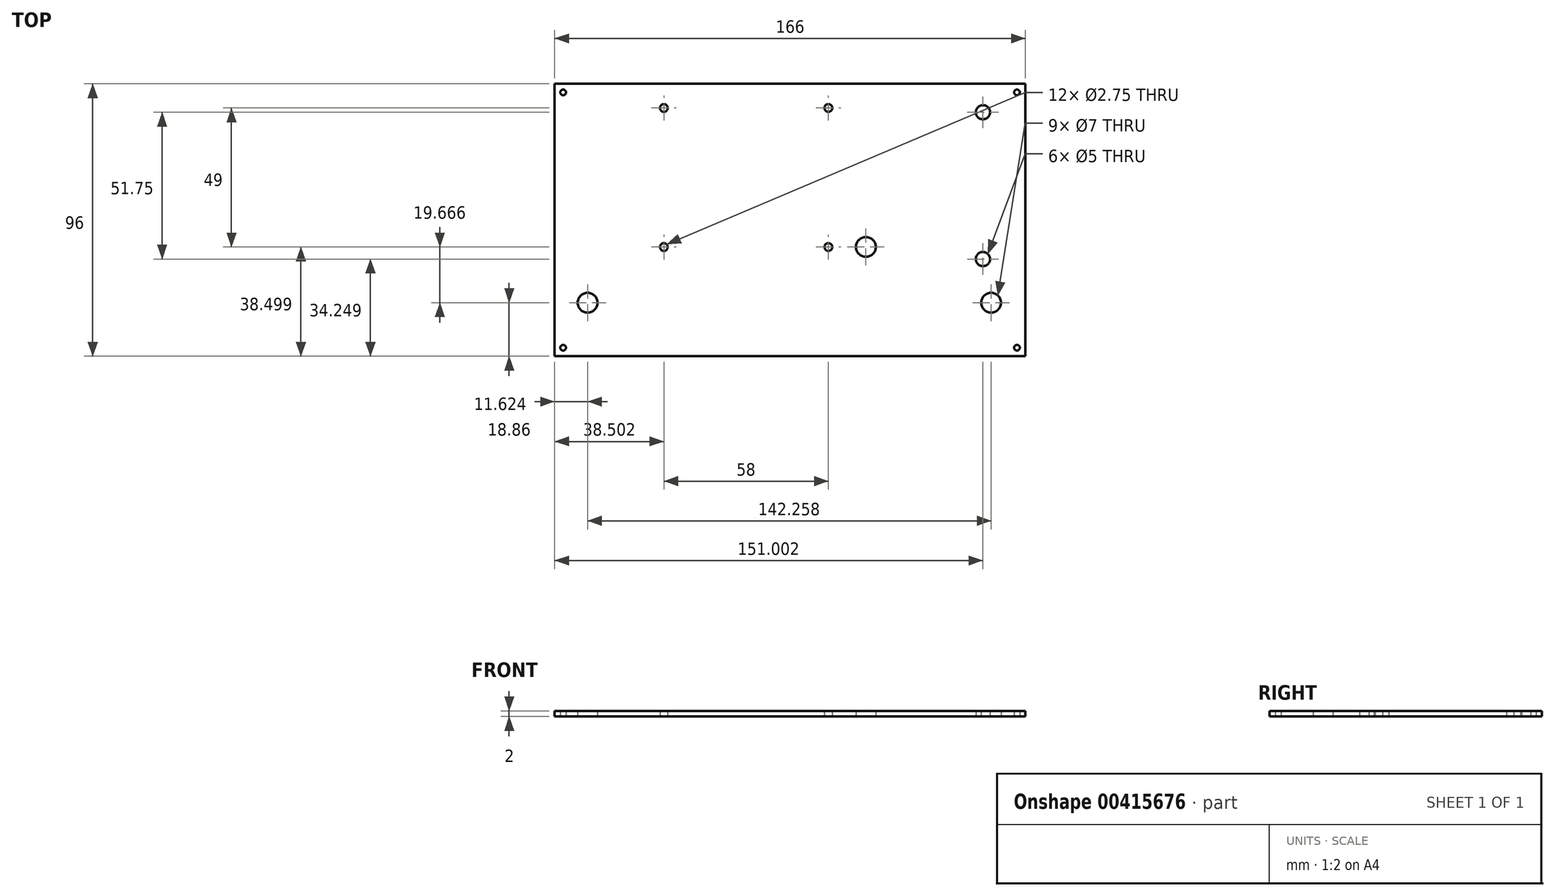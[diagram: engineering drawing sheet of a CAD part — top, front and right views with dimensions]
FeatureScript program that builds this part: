
annotation { "Feature Type Name" : "Feature", "Feature Type Description" : "" }
export const myFeature = defineFeature(function(context is Context, id is Id, definition is map)
    precondition{}
    {
        {
            var Q0;
            Q0=qCreatedBy(makeId("Top.planeOp"),FACE);
            var sketch = newSketch(context, id + "F0", { "sketchPlane" : qUnion([Q0])});
            skCircle(sketch, "E0", {"center": v(-64.72, 66.66) * mm, "radius": 1 * mm});
            skCircle(sketch, "E1", {"center": v(-64.72, -23.34) * mm, "radius": 1 * mm});
            skCircle(sketch, "E2", {"center": v(95.28, 66.66) * mm, "radius": 1 * mm});
            skCircle(sketch, "E3", {"center": v(95.28, -23.34) * mm, "radius": 1 * mm});
            skLineSegment(sketch, "E4.bottom", {"start": v(-67.72, 69.66) * mm, "end": v(98.28, 69.66) * mm});
            skLineSegment(sketch, "E4.top", {"start": v(-67.72, -26.34) * mm, "end": v(98.28, -26.34) * mm});
            skLineSegment(sketch, "E4.left", {"start": v(-67.72, 69.66) * mm, "end": v(-67.72, -26.34) * mm});
            skLineSegment(sketch, "E4.right", {"start": v(98.28, 69.66) * mm, "end": v(98.28, -26.34) * mm});
            skSolve(sketch);
        }
        {
            var Q0;
            Q0 = qSketchRegion(id + "F0", true);
            extrude(context, id + "F1", {"entities" : qUnion([Q0]), "depth" : 2 * mm, "offsetDistance" : 25 * mm});
        }
        {
            var Q0;
            Q0=qCreatedBy(makeId("Top.planeOp"),FACE);
            var sketch = newSketch(context, id + "F2", { "sketchPlane" : qUnion([Q0])});
            skLineSegment(sketch, "E5.bottom", {"start": v(29.28, 8.66) * mm, "end": v(-49.72, 8.66) * mm});
            skLineSegment(sketch, "E5.top", {"start": v(29.28, 64.66) * mm, "end": v(-49.72, 64.66) * mm});
            skLineSegment(sketch, "E5.left", {"start": v(32.28, 11.66) * mm, "end": v(32.28, 61.66) * mm});
            skLineSegment(sketch, "E5.right", {"start": v(-52.72, 11.66) * mm, "end": v(-52.72, 61.66) * mm});
            skPoint(sketch, "E6.visualSharp", {"position": v(32.28, 8.66) * mm});
            skArc(sketch, "E6.filletArc", {"start": v(29.28, 8.66) * mm, "mid": v(31.4, 9.54) * mm, "end": v(32.28, 11.66) * mm});
            skArc(sketch, "E7.filletArc", {"start": v(-52.72, 11.66) * mm, "mid": v(-51.84, 9.54) * mm, "end": v(-49.72, 8.66) * mm});
            skArc(sketch, "E8.filletArc", {"start": v(-49.72, 64.66) * mm, "mid": v(-51.84, 63.78) * mm, "end": v(-52.72, 61.66) * mm});
            skPoint(sketch, "E9.visualSharp", {"position": v(32.28, 64.66) * mm});
            skArc(sketch, "E9.filletArc", {"start": v(32.28, 61.66) * mm, "mid": v(31.4, 63.78) * mm, "end": v(29.28, 64.66) * mm});
            skCircle(sketch, "E10", {"center": v(28.78, 61.16) * mm, "radius": 1.38 * mm});
            skCircle(sketch, "E11", {"center": v(28.78, 12.16) * mm, "radius": 1.38 * mm});
            skCircle(sketch, "E12", {"center": v(-29.22, 12.16) * mm, "radius": 1.38 * mm});
            skCircle(sketch, "E13", {"center": v(-29.22, 61.16) * mm, "radius": 1.38 * mm});
            skLineSegment(sketch, "E14", {"start": v(-29.22, 61.16) * mm, "end": v(-29.22, 12.16) * mm, "construction": true});
            skCircle(sketch, "E15", {"center": v(83.28, 59.66) * mm, "radius": 2.5 * mm});
            skCircle(sketch, "E16", {"center": v(83.28, 7.9) * mm, "radius": 2.5 * mm});
            skLineSegment(sketch, "E17.bottom", {"start": v(-39.72, 5.66) * mm, "end": v(70.28, 5.66) * mm});
            skLineSegment(sketch, "E17.top", {"start": v(-39.72, -24.34) * mm, "end": v(70.28, -24.34) * mm});
            skLineSegment(sketch, "E17.left", {"start": v(-39.72, 5.66) * mm, "end": v(-39.72, -24.34) * mm});
            skLineSegment(sketch, "E17.right", {"start": v(70.28, 5.66) * mm, "end": v(70.28, -24.34) * mm});
            skLineSegment(sketch, "E18", {"start": v(-39.72, -11.85) * mm, "end": v(-67.72, -11.85) * mm, "construction": true});
            skLineSegment(sketch, "E19", {"start": v(70.28, -17.73) * mm, "end": v(98.28, -17.73) * mm, "construction": true});
            skCircle(sketch, "E20", {"center": v(42, 12.19) * mm, "radius": 3.5 * mm});
            skCircle(sketch, "E21", {"center": v(86.16, -7.48) * mm, "radius": 3.5 * mm});
            skCircle(sketch, "E22", {"center": v(-56.1, -7.48) * mm, "radius": 3.5 * mm});
            skLineSegment(sketch, "E23.bottom", {"start": v(72.28, 66.2) * mm, "end": v(94.28, 66.2) * mm, "construction": true});
            skLineSegment(sketch, "E23.top", {"start": v(72.28, 3.2) * mm, "end": v(94.28, 3.2) * mm, "construction": true});
            skLineSegment(sketch, "E23.left", {"start": v(72.28, 66.2) * mm, "end": v(72.28, 3.2) * mm, "construction": true});
            skLineSegment(sketch, "E23.right", {"start": v(94.28, 66.2) * mm, "end": v(94.28, 3.2) * mm, "construction": true});
            skSolve(sketch);
        }
        {
            var Q0;
            Q0=sQuery(id+"F2.wireOp",VERTEX,"E15.center");
            var Q1;
            Q1=sQuery(id+"F2.wireOp",VERTEX,"E16.center");
            var Q2;
            Q2=makeQuery(id+"F1.opExtrude","SWEPT_BODY",BODY,{"disambiguationData":[OSD([sQuery(id+"F0.wireOp",EDGE,"E0"),sQuery(id+"F0.wireOp",EDGE,"E1"),sQuery(id+"F0.wireOp",EDGE,"E2"),sQuery(id+"F0.wireOp",EDGE,"E3"),sQuery(id+"F0.wireOp",EDGE,"E4.bottom"),sQuery(id+"F0.wireOp",EDGE,"E4.top"),sQuery(id+"F0.wireOp",EDGE,"E4.left"),sQuery(id+"F0.wireOp",EDGE,"E4.right")])]});
            hole(context, id + "F3", {"style" : HoleStyle.SIMPLE, "endStyle" : HoleEndStyle.BLIND, "oppositeDirection" : true, "holeDiameter" : 5 * mm, "majorDiameter" : 5 * mm, "holeDepth" : 12 * mm, "isTappedThrough" : true, "tappedDepth" : 12 * mm, "tapClearance" : 3, "locations" : qUnion([Q0, Q1]), "scope" : qUnion([Q2])});
        }
        {
            var Q0;
            Q0=sQuery(id+"F2.wireOp",VERTEX,"E14.start");
            var Q1;
            Q1=sQuery(id+"F2.wireOp",VERTEX,"E14.end");
            var Q2;
            Q2=sQuery(id+"F2.wireOp",VERTEX,"E11.center");
            var Q3;
            Q3=sQuery(id+"F2.wireOp",VERTEX,"E10.center");
            var Q4;
            Q4=makeQuery(id+"F1.opExtrude","SWEPT_BODY",BODY,{"disambiguationData":[OSD([sQuery(id+"F0.wireOp",EDGE,"E0"),sQuery(id+"F0.wireOp",EDGE,"E1"),sQuery(id+"F0.wireOp",EDGE,"E2"),sQuery(id+"F0.wireOp",EDGE,"E3"),sQuery(id+"F0.wireOp",EDGE,"E4.bottom"),sQuery(id+"F0.wireOp",EDGE,"E4.top"),sQuery(id+"F0.wireOp",EDGE,"E4.left"),sQuery(id+"F0.wireOp",EDGE,"E4.right")])]});
            hole(context, id + "F4", {"style" : HoleStyle.SIMPLE, "endStyle" : HoleEndStyle.BLIND, "oppositeDirection" : true, "holeDiameter" : 2.75 * mm, "majorDiameter" : 5 * mm, "holeDepth" : 12 * mm, "isTappedThrough" : true, "tappedDepth" : 12 * mm, "tapClearance" : 3, "locations" : qUnion([Q0, Q1, Q2, Q3]), "scope" : qUnion([Q4])});
        }
        {
            var Q0;
            Q0=sQuery(id+"F2.wireOp",VERTEX,"E22.center");
            var Q1;
            Q1=sQuery(id+"F2.wireOp",VERTEX,"E21.center");
            var Q2;
            Q2=sQuery(id+"F2.wireOp",VERTEX,"E20.center");
            var Q3;
            Q3=makeQuery(id+"F1.opExtrude","SWEPT_BODY",BODY,{"disambiguationData":[OSD([sQuery(id+"F0.wireOp",EDGE,"E0"),sQuery(id+"F0.wireOp",EDGE,"E1"),sQuery(id+"F0.wireOp",EDGE,"E2"),sQuery(id+"F0.wireOp",EDGE,"E3"),sQuery(id+"F0.wireOp",EDGE,"E4.bottom"),sQuery(id+"F0.wireOp",EDGE,"E4.top"),sQuery(id+"F0.wireOp",EDGE,"E4.left"),sQuery(id+"F0.wireOp",EDGE,"E4.right")])]});
            hole(context, id + "F5", {"style" : HoleStyle.SIMPLE, "endStyle" : HoleEndStyle.BLIND, "oppositeDirection" : true, "holeDiameter" : 7 * mm, "majorDiameter" : 5 * mm, "holeDepth" : 12 * mm, "isTappedThrough" : true, "tappedDepth" : 12 * mm, "tapClearance" : 3, "locations" : qUnion([Q0, Q1, Q2]), "scope" : qUnion([Q3])});
        }
    });
